# Revit family: 36-52-116 DN400-500
name_source: partatom
category: Pipe Accessories
units: mm (PartAtom-declared; Revit-internal decimal feet)

## family parameters
Always vertical = No
Cut with Voids When Loaded = No
Part Type = Valve - Breaks Into
Round Connector Dimension = Use Diameter
Shared = No
Work Plane-Based = No

## types (5) — shared parameters
2 = 2 mm  [stored 0.00656168 ft]
36-400-52-161086 = DN400_D400
36-450-52-161086 = DN400_D450
36-500-52-161086 = DN400_D500
36-560-52-161086 = DN500_D560
36-630-52-161086 = DN500_D630
Bonnet_Dim4 = 55.32 mm
Description_ = AVK GATE VALVE, PREMIUM 100, PE PIPE ENDS, PN16
F1 = 37 mm  [stored 0.121391 ft]
Raised_dis = 4 mm  [stored 0.0131234 ft]
Search_table = 36-52-116 DN400-500
Stem1 = 48.1 mm  [stored 0.157808 ft]
Thickness = 9 mm  [stored 0.0295276 ft]
URL product pages = https://www.avkvalves.com
zero-valued in all types: Default Elevation

## per-type parameters (varying)
- DN400_D400: Body_Height=485 mm; Body_L=238 mm; Body_Rib_H=247 mm; Body_Rib_L=300 mm; Body_Rib_Start=60 mm  [stored 0.19685 ft]; Body_Rib_T=16 mm  [stored 0.0524934 ft]; Body_W=86 mm; Body_dim=70 mm  [stored 0.229659 ft]; Body_dim3=261.8 mm; Body_dim4=94.6 mm; Body_dimension1=33.6 mm  [stored 0.110236 ft]; Body_dimension2=127.5 mm; Bonnet_FL_L=282 mm; Bonnet_FL_T=15 mm  [stored 0.0492126 ft]; Bonnet_FL_W=141 mm; Bonnet_dim1=273.7 mm; Bonnet_dim2=68.8 mm; Bonnet_dim3=48.16 mm  [stored 0.158005 ft]; Bonnet_dim4=61.92 mm  [stored 0.20315 ft]; Bore=200 mm; Bottom_revolve=166.6 mm; D=200 mm; DN=400 mm; Dd=200 mm; F=32 mm  [stored 0.104987 ft]; F2=55 mm  [stored 0.180446 ft]; FL_T=28 mm  [stored 0.0918635 ft]; Fillet=54 mm  [stored 0.177165 ft]; Fillet1=64.8 mm  [stored 0.212598 ft]; Fitting_dim1=64.59 mm; Fitting_dim2=96.88 mm; Fitting_dim3=116.26 mm; Fitting_dim4=121.1 mm; Fitting_mid_L=215.29 mm; Gate valve_Pipe_L=140 mm; H=912 mm; H3=1165 mm; H3-H=253 mm; L=1700 mm; L1=355 mm; OD=290 mm; Raised_R=241 mm; Rib1_H=75 mm  [stored 0.246063 ft]; Rib1_L=282.5 mm; Rib1_W=140 mm; Rib2_H=195 mm; Rib2_L=282.5 mm; Rib2_W=140 mm; Rib3_H=315 mm; Rib3_L=282.5 mm; Rib3_W=140 mm; Rib4_H=485 mm; Rib4_L=282.5 mm; Rib4_W=140 mm; Rib_dim1=112 mm; Rib_dim2=140 mm; Rib_t=8 mm  [stored 0.0262467 ft]; Valve_D=214 mm; Valve_D1=194 mm; W=285 mm; axis_dim=209 mm; body_dim=202.3 mm; cut=0 mm  [stored 0 ft]; slant=340 mm; stem1=32 mm  [stored 0.104987 ft]
- DN400_D450: Body_Height=485 mm; Body_L=238 mm; Body_Rib_H=247 mm; Body_Rib_L=300 mm; Body_Rib_Start=60 mm  [stored 0.19685 ft]; Body_Rib_T=16 mm  [stored 0.0524934 ft]; Body_W=86 mm; Body_dim=70 mm  [stored 0.229659 ft]; Body_dim3=261.8 mm; Body_dim4=94.6 mm; Body_dimension1=33.6 mm  [stored 0.110236 ft]; Body_dimension2=127.5 mm; Bonnet_FL_L=282 mm; Bonnet_FL_T=15 mm  [stored 0.0492126 ft]; Bonnet_FL_W=141 mm; Bonnet_dim1=273.7 mm; Bonnet_dim2=68.8 mm; Bonnet_dim3=48.16 mm  [stored 0.158005 ft]; Bonnet_dim4=61.92 mm  [stored 0.20315 ft]; Bore=200.05 mm; Bottom_revolve=166.6 mm; D=225 mm; DN=400.1 mm; Dd=200.05 mm; F=32 mm  [stored 0.104987 ft]; F2=55 mm  [stored 0.180446 ft]; FL_T=28 mm  [stored 0.0918635 ft]; Fillet=54 mm  [stored 0.177165 ft]; Fillet1=64.8 mm  [stored 0.212598 ft]; Fitting_dim1=68.29 mm; Fitting_dim2=102.44 mm; Fitting_dim3=122.93 mm; Fitting_dim4=128.05 mm; Fitting_mid_L=227.65 mm; Gate valve_Pipe_L=140 mm; H=935 mm; H3=1200 mm; H3-H=265 mm; L=1800 mm; L1=384 mm; OD=290 mm; Raised_R=241 mm; Rib1_H=75 mm  [stored 0.246063 ft]; Rib1_L=282.5 mm; Rib1_W=140 mm; Rib2_H=195 mm; Rib2_L=282.5 mm; Rib2_W=140 mm; Rib3_H=315 mm; Rib3_L=282.5 mm; Rib3_W=140 mm; Rib4_H=485 mm; Rib4_L=282.5 mm; Rib4_W=140 mm; Rib_dim1=112.03 mm; Rib_dim2=140.04 mm; Rib_t=8 mm  [stored 0.0262467 ft]; Valve_D=214.05 mm; Valve_D1=194.05 mm; W=285 mm; axis_dim=209.05 mm; body_dim=202.3 mm; cut=24.95 mm  [stored 0.081857 ft]; slant=360 mm; stem1=75 mm  [stored 0.246063 ft]
- DN400_D500: Body_Height=485 mm; Body_L=238 mm; Body_Rib_H=247 mm; Body_Rib_L=300 mm; Body_Rib_Start=60 mm  [stored 0.19685 ft]; Body_Rib_T=16 mm  [stored 0.0524934 ft]; Body_W=86 mm; Body_dim=70 mm  [stored 0.229659 ft]; Body_dim3=261.8 mm; Body_dim4=94.6 mm; Body_dimension1=34.8 mm  [stored 0.114173 ft]; Body_dimension2=127.5 mm; Bonnet_FL_L=282 mm; Bonnet_FL_T=16 mm  [stored 0.0524934 ft]; Bonnet_FL_W=141 mm; Bonnet_dim1=273.7 mm; Bonnet_dim2=68.8 mm; Bonnet_dim3=48.16 mm  [stored 0.158005 ft]; Bonnet_dim4=61.92 mm  [stored 0.20315 ft]; Bore=200.06 mm; Bottom_revolve=166.6 mm; D=250 mm; DN=400.11 mm; Dd=200.06 mm; F=32 mm  [stored 0.104987 ft]; F2=55 mm  [stored 0.180446 ft]; FL_T=29 mm  [stored 0.0951444 ft]; Fillet=54 mm  [stored 0.177165 ft]; Fillet1=64.8 mm  [stored 0.212598 ft]; Fitting_dim1=78.35 mm; Fitting_dim2=117.53 mm; Fitting_dim3=141.04 mm; Fitting_dim4=146.91 mm; Fitting_mid_L=261.18 mm; Gate valve_Pipe_L=140 mm; H=951 mm; H3=1246 mm; H3-H=295 mm; L=1850 mm; L1=350 mm; OD=320 mm; Raised_R=280 mm; Rib1_H=75 mm  [stored 0.246063 ft]; Rib1_L=282.5 mm; Rib1_W=140 mm; Rib2_H=195 mm; Rib2_L=282.5 mm; Rib2_W=140 mm; Rib3_H=315 mm; Rib3_L=282.5 mm; Rib3_W=140 mm; Rib4_H=485 mm; Rib4_L=282.5 mm; Rib4_W=140 mm; Rib_dim1=112.03 mm; Rib_dim2=140.04 mm; Rib_t=8 mm  [stored 0.0262467 ft]; Valve_D=214.06 mm; Valve_D1=194.06 mm; W=300 mm; axis_dim=209.06 mm; body_dim=202.3 mm; cut=49.95 mm; slant=370 mm; stem1=75 mm  [stored 0.246063 ft]
- DN500_D560: Body_Height=580 mm; Body_L=381 mm; Body_Rib_H=330 mm; Body_Rib_L=400 mm; Body_Rib_Start=134 mm; Body_Rib_T=20 mm  [stored 0.0656168 ft]; Body_W=149.5 mm; Body_dim=80 mm  [stored 0.262467 ft]; Body_dim3=419.1 mm; Body_dim4=164.45 mm; Body_dimension1=34.8 mm  [stored 0.114173 ft]; Body_dimension2=127.5 mm; Bonnet_FL_L=418 mm; Bonnet_FL_T=20 mm  [stored 0.0656168 ft]; Bonnet_FL_W=170 mm; Bonnet_dim1=438.15 mm; Bonnet_dim2=119.6 mm; Bonnet_dim3=83.72 mm; Bonnet_dim4=107.64 mm; Bore=250 mm; Bottom_revolve=266.7 mm; D=280 mm; DN=500 mm; Dd=250 mm; F=30 mm  [stored 0.0984252 ft]; F2=75 mm  [stored 0.246063 ft]; FL_T=29 mm  [stored 0.0951444 ft]; Fillet=54 mm  [stored 0.177165 ft]; Fillet1=64.8 mm  [stored 0.212598 ft]; Fitting_dim1=75.44 mm; Fitting_dim2=113.16 mm; Fitting_dim3=135.79 mm; Fitting_dim4=141.45 mm; Fitting_mid_L=251.47 mm; Gate valve_Pipe_L=225 mm; H=1118 mm; H3=1448 mm; H3-H=330 mm; L=2200 mm; L1=474 mm; OD=320 mm; Raised_R=280 mm; Rib1_H=120 mm; Rib1_L=418 mm; Rib1_W=170 mm; Rib2_H=222 mm; Rib2_L=418 mm; Rib2_W=170 mm; Rib3_H=340 mm; Rib3_L=418 mm; Rib3_W=170 mm; Rib4_H=550 mm; Rib4_L=418 mm; Rib4_W=170 mm; Rib_dim1=140 mm; Rib_dim2=175 mm; Rib_t=10 mm  [stored 0.0328084 ft]; Valve_D=264 mm; Valve_D1=244 mm; W=300 mm; axis_dim=259 mm; body_dim=323.85 mm; cut=30 mm  [stored 0.0984252 ft]; slant=440 mm; stem1=30 mm  [stored 0.0984252 ft]
- DN500_D630: Body_Height=580 mm; Body_L=381 mm; Body_Rib_H=330 mm; Body_Rib_L=400 mm; Body_Rib_Start=134 mm; Body_Rib_T=20 mm  [stored 0.0656168 ft]; Body_W=149.5 mm; Body_dim=80 mm  [stored 0.262467 ft]; Body_dim3=419.1 mm; Body_dim4=164.45 mm; Body_dimension1=37.2 mm  [stored 0.122047 ft]; Body_dimension2=131.75 mm; Bonnet_FL_L=418 mm; Bonnet_FL_T=20 mm  [stored 0.0656168 ft]; Bonnet_FL_W=170 mm; Bonnet_dim1=438.15 mm; Bonnet_dim2=119.6 mm; Bonnet_dim3=83.72 mm; Bonnet_dim4=107.64 mm; Bore=250.05 mm; Bottom_revolve=266.7 mm; D=315 mm; DN=500.1 mm; Dd=250.05 mm; F=30 mm  [stored 0.0984252 ft]; F2=75 mm  [stored 0.246063 ft]; FL_T=31 mm  [stored 0.101706 ft]; Fillet=58 mm  [stored 0.190289 ft]; Fillet1=69.6 mm  [stored 0.228346 ft]; Fitting_dim1=77.74 mm; Fitting_dim2=116.6 mm; Fitting_dim3=139.92 mm; Fitting_dim4=145.75 mm; Fitting_mid_L=259.12 mm; Gate valve_Pipe_L=225 mm; H=1136 mm; H3=1502 mm; H3-H=366 mm; L=2350 mm; L1=534 mm; OD=357.5 mm; Raised_R=295 mm; Rib1_H=120 mm; Rib1_L=418 mm; Rib1_W=170 mm; Rib2_H=222 mm; Rib2_L=418 mm; Rib2_W=170 mm; Rib3_H=340 mm; Rib3_L=418 mm; Rib3_W=170 mm; Rib4_H=550 mm; Rib4_L=418 mm; Rib4_W=170 mm; Rib_dim1=140.03 mm; Rib_dim2=175.04 mm; Rib_t=10 mm  [stored 0.0328084 ft]; Valve_D=264.05 mm; Valve_D1=244.05 mm; W=310 mm; axis_dim=259.05 mm; body_dim=323.85 mm; cut=64.95 mm  [stored 0.213091 ft]; slant=470 mm; stem1=30 mm  [stored 0.0984252 ft]

note: [stored X ft] marks values corroborated as IEEE doubles in the binary element streams (Revit-internal decimal feet)

## geometry (parser evidence)
native form markers: Sweep x10
no freeform markers — native parametric forms only
